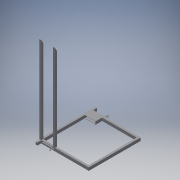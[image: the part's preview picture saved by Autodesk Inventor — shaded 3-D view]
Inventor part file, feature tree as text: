
AUTODESK INVENTOR PART (.ipt)
format: ipt  version: 2018.3 (Build 223284000, 284)  size: 238,592 bytes
history: native  units: mm
features: extrude x9, sketch x9, chamfer x2
ambient origin geometry x8: Origin, YZ Plane, XZ Plane, XY Plane, X Axis, Y Axis, Z Axis, Center Point
bodies: Solid1 (feature_tree)
feature tree (20):
  extrude  "Extrusion1"  Depth=52.5mm
  extrude  "Extrusion2"  Depth=46.0mm
  extrude  "Extrusion3"  Depth=10.0mm TaperAngle=0.0deg
  chamfer  "Chamfer1"  Distance=87.5mm
  chamfer  "Chamfer2"  Distance=2.0mm Angle=60.0deg
  extrude  "Extrusion4"  Depth=10.0mm
  extrude  "Extrusion5"  Depth=1.5mm
  extrude  "Extrusion6"  Depth=10.0mm TaperAngle=0.0deg
  extrude  "Extrusion7"  Depth=1.8mm
  sketch  "Sketch8"  dims[d21=2.85mm d22=10.0mm d23=0.0mm]
  sketch  "Sketch9"  dims[d24=1.0mm d25=1.8mm d26=0.85mm d27=1.25mm d28=1.8mm d29=2.6mm d30=2.6mm d31=1.0mm d32=1.0mm d33=0.5mm d35=4.0mm d36=0.0mm d49=4.0mm d50=0.0mm d51=10.66mm d52=2.54mm d54=0.23mm d55=2.0mm d57=0.23mm d58=6.5mm d59=0.0mm d60=2.0mm d61=30.0deg d62=2.0mm d63=60.0deg d64=0.5mm d65=35.371384mm d74=2.0mm d75=3.0mm d76=0.0mm d77=0.0mm d78=0.0mm d79=0.0mm d81=1.5mm d82=2.0mm d94=0.5mm d95=0.25mm d96=4.0mm d97=0.0mm d98=1.311971mm d99=0.1535mm d100=0.1535mm d101=4.0mm d102=0.0mm d103=0.2mm d104=0.2mm]
  extrude  "Extrusion10"  Depth=0.85mm
  extrude  "Extrusion11"  Depth=1.25mm
  sketch  "Sketch1"  dims[d0=50.0mm d1=52.5mm]
  sketch  "Sketch2"  dims[d2=3.0mm d3=0.0mm d4=46.0mm]
  sketch  "Sketch3"  dims[d5=48.5mm d6=10.0mm d7=0.0mm]
  sketch  "Sketch4"  dims[d8=2.0mm]
  sketch  "Sketch5"  dims[d9=11.7mm d10=87.5mm d11=0.0mm d12=2.0mm d13=2.0mm d14=60.0deg]
  sketch  "Sketch6"  dims[d15=2.0mm d16=2.0mm d17=60.0deg d18=10.0mm]
  sketch  "Sketch7"  dims[d19=1.0mm d20=1.5mm]
